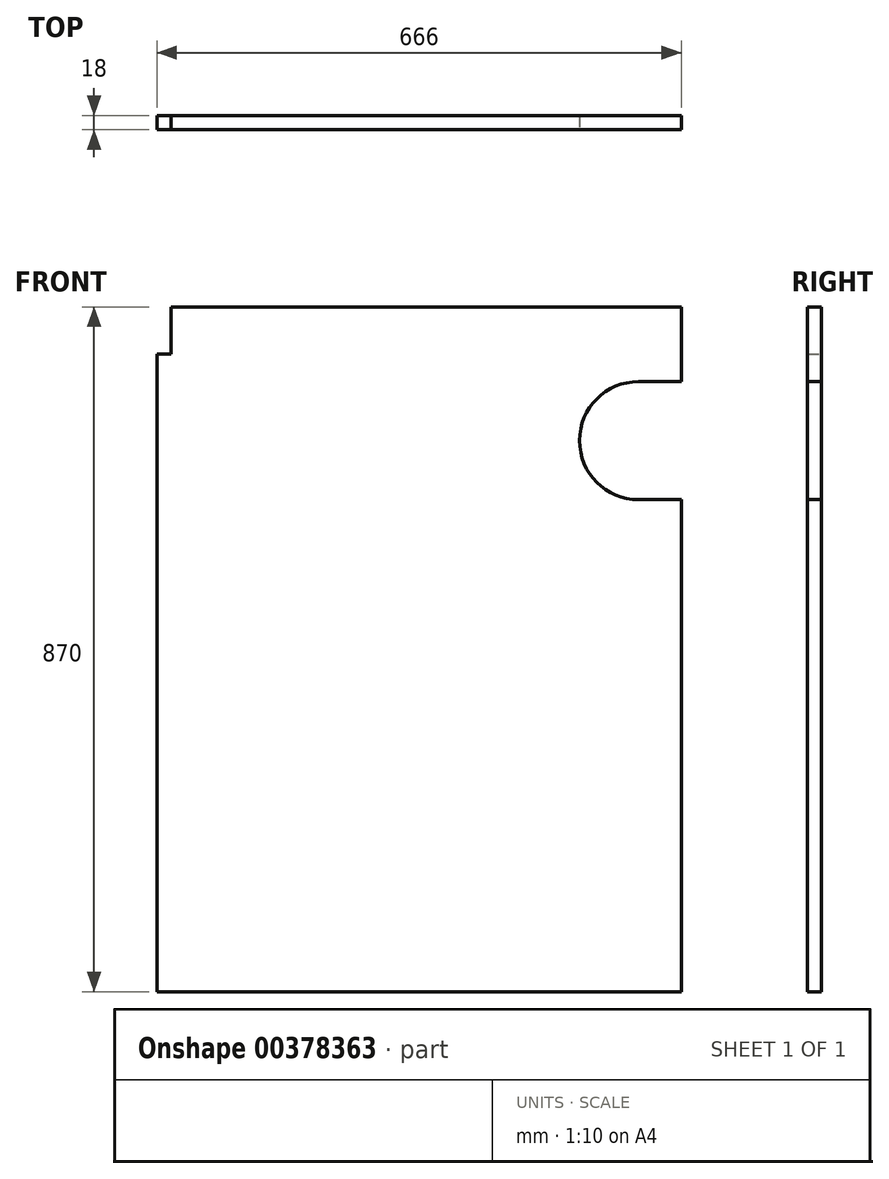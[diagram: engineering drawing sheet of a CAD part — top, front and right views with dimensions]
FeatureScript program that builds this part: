
annotation { "Feature Type Name" : "Feature", "Feature Type Description" : "" }
export const myFeature = defineFeature(function(context is Context, id is Id, definition is map)
    precondition{}
    {
        {
            var Q0;
            Q0=qCreatedBy(makeId("Front.planeOp"),FACE);
            var sketch = newSketch(context, id + "F0", { "sketchPlane" : qUnion([Q0])});
            skLineSegment(sketch, "E0.bottom", {"start": v(333, 435) * mm, "end": v(-315, 435) * mm});
            skLineSegment(sketch, "E0.top", {"start": v(333, -435) * mm, "end": v(-333, -435) * mm});
            skLineSegment(sketch, "E0.left", {"start": v(333, 435) * mm, "end": v(333, -435) * mm});
            skLineSegment(sketch, "E0.right", {"start": v(-333, 375) * mm, "end": v(-333, -435) * mm});
            skPoint(sketch, "E0.middle", {"position": v(0, 0) * mm});
            skLineSegment(sketch, "E1", {"start": v(-315, 435) * mm, "end": v(-315, 375) * mm});
            skLineSegment(sketch, "E2", {"start": v(-315, 375) * mm, "end": v(-333, 375) * mm});
            skSolve(sketch);
        }
        {
            var Q0;
            Q0=makeQuery(id+"F0.imprint","IMPRINT",FACE,{"disambiguationData":[TD([[makeQuery(id+"F0.imprint","IMPRINT",EDGE,{"derivedFrom":sQuery(id+"F0.wireOp",EDGE,"E0.bottom")}),1.0]])]});
            extrude(context, id + "F1", {"entities" : qUnion([Q0]), "depth" : 18 * mm});
        }
        {
            var Q0;
            Q0=makeQuery(id+"F1.opExtrude","CAP_FACE",FACE,{"disambiguationData":[OSD([sQuery(id+"F0.wireOp",EDGE,"E0.bottom"),sQuery(id+"F0.wireOp",EDGE,"E0.top"),sQuery(id+"F0.wireOp",EDGE,"E0.left"),sQuery(id+"F0.wireOp",EDGE,"E0.right"),sQuery(id+"F0.wireOp",EDGE,"E1"),sQuery(id+"F0.wireOp",EDGE,"E2")])],"isStart":false});
            var sketch = newSketch(context, id + "F2", { "sketchPlane" : qUnion([Q0])});
            skArc(sketch, "E3", {"start": v(278.8, 340) * mm, "mid": v(203.8, 265) * mm, "end": v(278.8, 190) * mm});
            skLineSegment(sketch, "E4", {"start": v(278.8, 340) * mm, "end": v(333, 340) * mm});
            skLineSegment(sketch, "E5", {"start": v(278.8, 190) * mm, "end": v(333, 190) * mm});
            skLineSegment(sketch, "E6", {"start": v(333, 340) * mm, "end": v(333, 190) * mm});
            skSolve(sketch);
        }
        {
            var Q0;
            Q0 = qSketchRegion(id + "F2", true);
            extrude(context, id + "F3", {"entities" : qUnion([Q0]), "operationType" : NewBodyOperationType.REMOVE, "oppositeDirection" : true, "depth" : 18 * mm});
        }
    });
